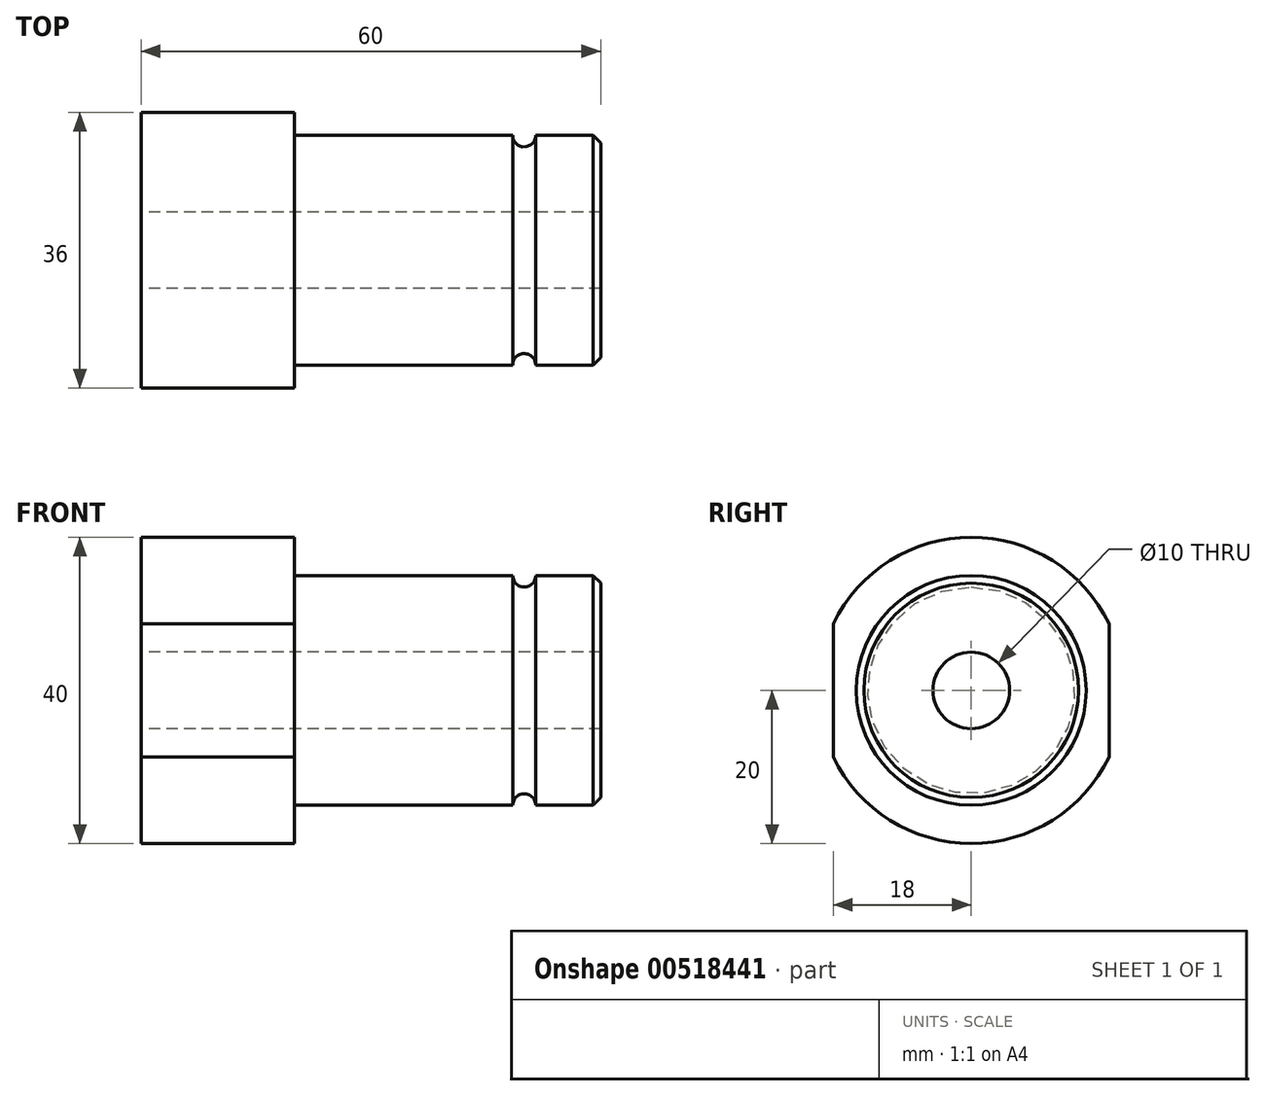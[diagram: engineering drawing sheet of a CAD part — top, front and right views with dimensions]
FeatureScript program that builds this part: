
annotation { "Feature Type Name" : "Feature", "Feature Type Description" : "" }
export const myFeature = defineFeature(function(context is Context, id is Id, definition is map)
    precondition{}
    {
        {
            assignVariable(context, id + "F0", {"name" : "A", "anyValue" : 40});
        }
        {
            var Q0;
            Q0=qCreatedBy(makeId("Right.planeOp"),FACE);
            var sketch = newSketch(context, id + "F1", { "sketchPlane" : qUnion([Q0])});
            skCircle(sketch, "E0", {"center": v(0, 0) * mm, "radius": 20 * mm});
            skCircle(sketch, "E1", {"center": v(0, 0) * mm, "radius": 5 * mm});
            skSolve(sketch);
        }
        {
            var Q0;
            Q0 = qSketchRegion(id + "F1", true);
            extrude(context, id + "F2", {"entities" : qUnion([Q0]), "depth" : 20 * mm, "offsetDistance" : 25 * mm});
        }
        {
            var Q0;
            Q0=makeQuery(id+"F2.opExtrude","CAP_FACE",FACE,{"disambiguationData":[OSD([sQuery(id+"F1.wireOp",EDGE,"E0"),sQuery(id+"F1.wireOp",EDGE,"E1")])],"isStart":false});
            var sketch = newSketch(context, id + "F3", { "sketchPlane" : qUnion([Q0])});
            skCircle(sketch, "E2", {"center": v(0, 0) * mm, "radius": 15 * mm});
            skSolve(sketch);
        }
        {
            var Q0;
            Q0 = qSketchRegion(id + "F3", true);
            extrude(context, id + "F4", {"entities" : qUnion([Q0]), "operationType" : NewBodyOperationType.ADD, "depth" : (getVariable(context, 'A')) * mm, "offsetDistance" : 25 * mm});
        }
        {
            var Q0;
            Q0=makeQuery(id+"F4.opExtrude","CAP_FACE",FACE,{"disambiguationData":[OSD([sQuery(id+"F3.wireOp",EDGE,"E2")])],"isStart":false});
            var sketch = newSketch(context, id + "F5", { "sketchPlane" : qUnion([Q0])});
            skCircle(sketch, "E3", {"center": v(0, 0) * mm, "radius": 5 * mm});
            skSolve(sketch);
        }
        {
            var Q0;
            Q0 = qSketchRegion(id + "F5", true);
            extrude(context, id + "F6", {"entities" : qUnion([Q0]), "operationType" : NewBodyOperationType.REMOVE, "endBound" : BoundingType.THROUGH_ALL, "oppositeDirection" : true, "depth" : 25 * mm, "offsetDistance" : 25 * mm});
        }
        {
            var Q0;
            Q0=makeQuery(id+"F4.opExtrude","CAP_EDGE",EDGE,{"disambiguationData":[OSD([sQuery(id+"F3.wireOp",EDGE,"E2")])],"isStart":false});
            chamfer(context, id + "F7", {"entities" : qUnion([Q0]), "width" : 1 * mm, "tangentPropagation" : true});
        }
        {
            var Q0;
            Q0=qCreatedBy(makeId("Right.planeOp"),FACE);
            var sketch = newSketch(context, id + "F8", { "sketchPlane" : qUnion([Q0])});
            skLineSegment(sketch, "E4.bottom", {"start": v(-18, 20) * mm, "end": v(18, 20) * mm});
            skLineSegment(sketch, "E4.top", {"start": v(-18, -20) * mm, "end": v(18, -20) * mm});
            skLineSegment(sketch, "E4.left", {"start": v(-18, 20) * mm, "end": v(-18, -20) * mm});
            skLineSegment(sketch, "E4.right", {"start": v(18, 20) * mm, "end": v(18, -20) * mm});
            skPoint(sketch, "E4.middle", {"position": v(0, 0) * mm});
            skCircle(sketch, "E5.0", {"center": v(0, 0) * mm, "radius": 20 * mm});
            skSolve(sketch);
        }
        {
            var Q0;
            {var subQ0=sQuery(id+"F8.wireOp",EDGE,"E5.0");var subQ1=sQuery(id+"F8.wireOp",EDGE,"E4.right");var subQ2=makeQuery(id+"F8.imprint","INTERSECT",VERTEX,{"disambiguationData":[OD(0.0)],"derivedFrom":[subQ1,subQ0]});Q0=makeQuery(id+"F8.imprint","IMPRINT",FACE,{"disambiguationData":[TD([[makeQuery(id+"F8.imprint","IMPRINT",EDGE,{"disambiguationData":[TD([[subQ2,-1.0]])],"derivedFrom":subQ1}),1.0]])]});}
            extrude(context, id + "F9", {"entities" : qUnion([Q0]), "operationType" : NewBodyOperationType.REMOVE, "depth" : 20 * mm, "offsetDistance" : 25 * mm});
        }
        {
            var Q0;
            {var subQ0=sQuery(id+"F8.wireOp",EDGE,"E5.0");var subQ1=sQuery(id+"F8.wireOp",EDGE,"E4.left");var subQ2=makeQuery(id+"F8.imprint","INTERSECT",VERTEX,{"disambiguationData":[OD(0.0)],"derivedFrom":[subQ1,subQ0]});Q0=makeQuery(id+"F8.imprint","IMPRINT",FACE,{"disambiguationData":[TD([[makeQuery(id+"F8.imprint","IMPRINT",EDGE,{"disambiguationData":[TD([[subQ2,-1.0]])],"derivedFrom":subQ1}),-1.0]])]});}
            extrude(context, id + "F10", {"entities" : qUnion([Q0]), "operationType" : NewBodyOperationType.REMOVE, "depth" : 20 * mm, "offsetDistance" : 25 * mm});
        }
        {
            var Q0;
            Q0=qCreatedBy(makeId("Front.planeOp"),FACE);
            var sketch = newSketch(context, id + "F11", { "sketchPlane" : qUnion([Q0])});
            skLineSegment(sketch, "E6", {"start": v(50, 15) * mm, "end": v(50, -15) * mm});
            skCircle(sketch, "E7", {"center": v(50, 15) * mm, "radius": 1.5 * mm});
            skSolve(sketch);
        }
        {
            var Q0;
            Q0=makeQuery(id+"F11.imprint","IMPRINT",FACE,{"disambiguationData":[TD([[makeQuery(id+"F11.imprint","IMPRINT",EDGE,{"derivedFrom":sQuery(id+"F11.wireOp",EDGE,"E7")}),1.0]])]});
            var Q1;
            Q1=makeQuery(id+"F4.opExtrude","SWEPT_FACE",FACE,{"disambiguationData":[OSD([sQuery(id+"F3.wireOp",EDGE,"E2")])]});
            revolve(context, id + "F12", {"operationType" : NewBodyOperationType.REMOVE, "entities" : qUnion([Q0]), "axis" : qUnion([Q1]), "revolveType" : RevolveType.FULL, "oppositeDirection" : true});
        }
        {
            var Q0;
            Q0=makeQuery(id+"F2.opExtrude","SWEPT_BODY",BODY,{"disambiguationData":[OSD([sQuery(id+"F1.wireOp",EDGE,"E0"),sQuery(id+"F1.wireOp",EDGE,"E1")])]});
            transform(context, id + "F13", {"entities" : qUnion([Q0]), "transformType" : TransformType.TRANSLATION_3D, "dx" : -2 * mm, "dy" : -80 * mm, "dz" : 0 * mm, "makeCopy" : true});
        }
        {
            var Q0;
            Q0=makeQuery(id+"F13.opPattern","COPY",BODY,{"derivedFrom":makeQuery(id+"F2.opExtrude","SWEPT_BODY",BODY,{"disambiguationData":[OSD([sQuery(id+"F1.wireOp",EDGE,"E0"),sQuery(id+"F1.wireOp",EDGE,"E1")])]}),"instanceName":"1"});
            deleteBodies(context, id + "F14", {"entities" : qUnion([Q0])});
        }
    });
